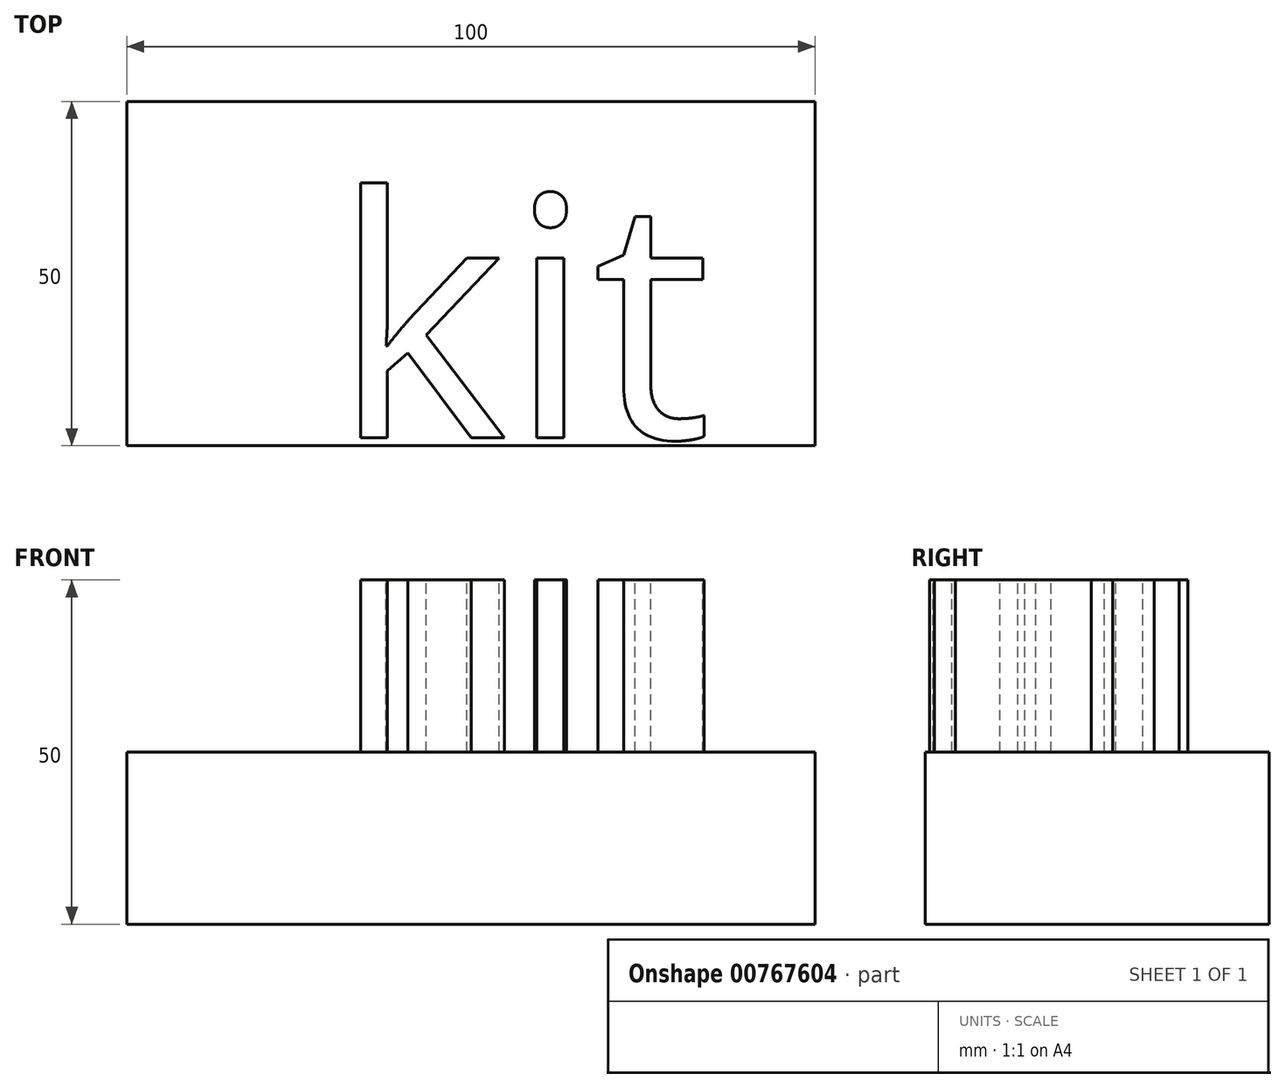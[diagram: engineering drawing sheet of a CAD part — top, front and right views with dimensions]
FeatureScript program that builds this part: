
annotation { "Feature Type Name" : "Feature", "Feature Type Description" : "" }
export const myFeature = defineFeature(function(context is Context, id is Id, definition is map)
    precondition{}
    {
        {
            var Q0;
            Q0=qCreatedBy(makeId("Top.planeOp"),FACE);
            var sketch = newSketch(context, id + "F0", { "sketchPlane" : qUnion([Q0])});
            skLineSegment(sketch, "E0.bottom", {"start": v(-56.47, 13.76) * mm, "end": v(43.53, 13.76) * mm});
            skLineSegment(sketch, "E0.top", {"start": v(-56.47, -36.24) * mm, "end": v(43.53, -36.24) * mm});
            skLineSegment(sketch, "E0.left", {"start": v(-56.47, 13.76) * mm, "end": v(-56.47, -36.24) * mm});
            skLineSegment(sketch, "E0.right", {"start": v(43.53, 13.76) * mm, "end": v(43.53, -36.24) * mm});
            skSolve(sketch);
        }
        {
            var Q0;
            Q0=makeQuery(id+"F0.imprint","IMPRINT",FACE,{"disambiguationData":[TD([[makeQuery(id+"F0.imprint","IMPRINT",EDGE,{"derivedFrom":sQuery(id+"F0.wireOp",EDGE,"E0.bottom")}),-1.0]])]});
            extrude(context, id + "F1", {"entities" : qUnion([Q0]), "depth" : 25 * mm, "offsetDistance" : 25 * mm});
        }
        {
            var Q0;
            Q0=qCreatedBy(makeId("Top.planeOp"),FACE);
            cPlane(context, id + "F2", {"entities" : qUnion([Q0]), "cplaneType" : CPlaneType.OFFSET, "offset" : 50 * mm, "width" : 150 * mm, "height" : 150 * mm});
        }
        {
            var Q0;
            Q0=qCreatedBy(id+"F2.planeOp",FACE);
            var sketch = newSketch(context, id + "F3", { "sketchPlane" : qUnion([Q0])});
            skText(sketch, "E1", { "text": "kit", "fontName": "OpenSans-Regular.ttf"});
            const initialGuessF3  = {"E1": [-0.02671, -0.03512, 1, 0, 0.03512]};
            skSetInitialGuess(sketch, initialGuessF3);
            skSolve(sketch);
        }
        {
            var Q0;
            Q0 = qSketchRegion(id + "F3", true);
            extrude(context, id + "F4", {"entities" : qUnion([Q0]), "endBound" : BoundingType.UP_TO_NEXT, "oppositeDirection" : true, "depth" : 25 * mm, "offsetDistance" : 25 * mm});
        }
    });
